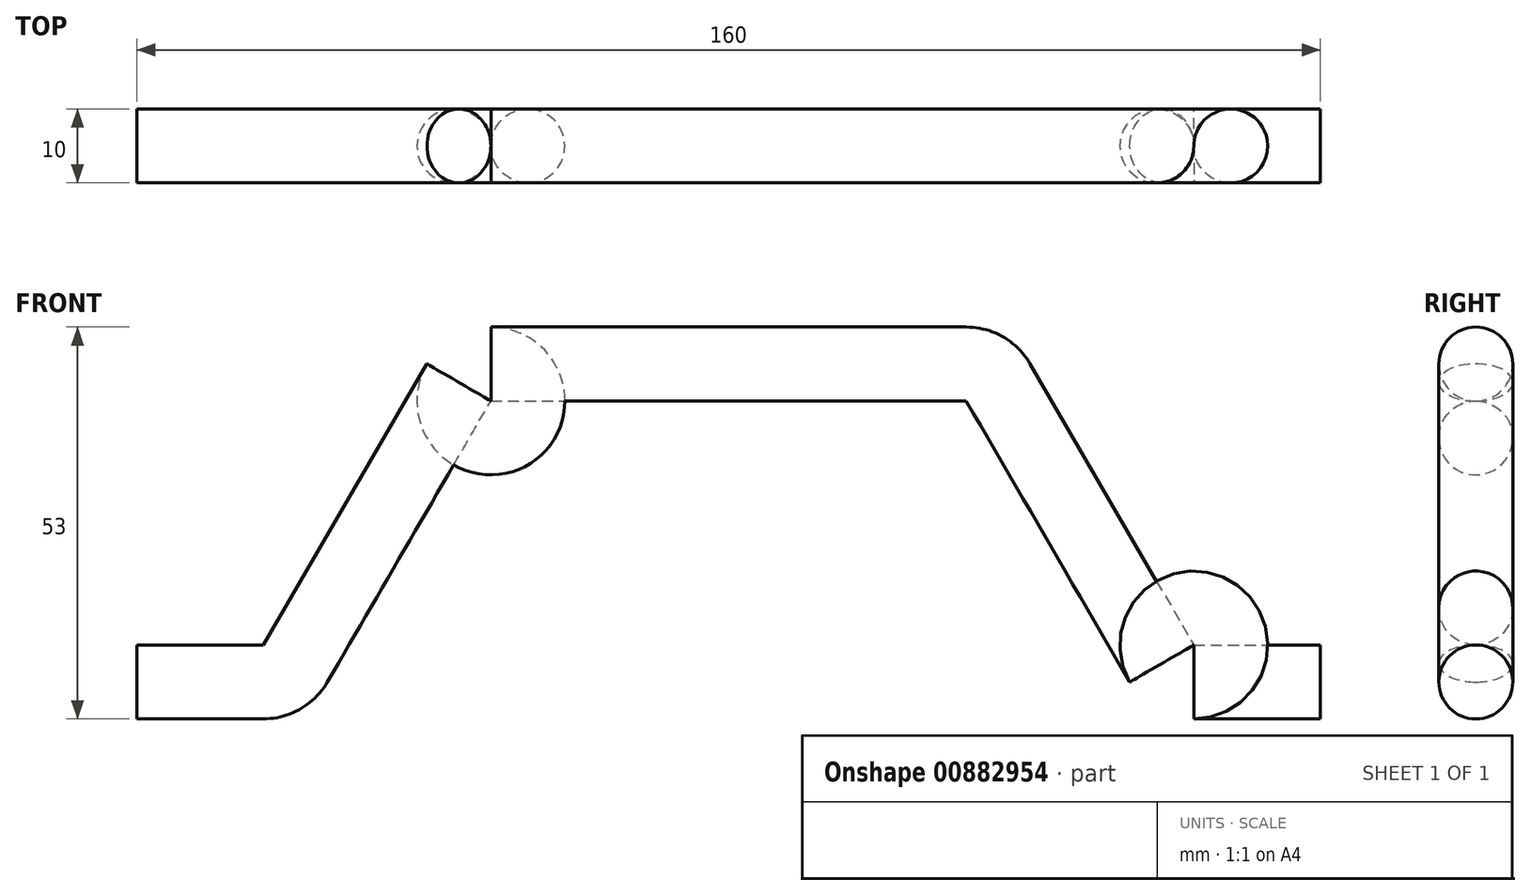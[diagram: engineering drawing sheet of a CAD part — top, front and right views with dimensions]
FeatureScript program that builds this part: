
annotation { "Feature Type Name" : "Feature", "Feature Type Description" : "" }
export const myFeature = defineFeature(function(context is Context, id is Id, definition is map)
    precondition{}
    {
        {
            var Q0;
            Q0=qCreatedBy(makeId("Front.planeOp"),FACE);
            var sketch = newSketch(context, id + "F0", { "sketchPlane" : qUnion([Q0])});
            skLineSegment(sketch, "E0.bottom", {"start": v(0, 0) * mm, "end": v(20, 0) * mm});
            skLineSegment(sketch, "E0.top", {"start": v(0, 5) * mm, "end": v(20, 5) * mm});
            skLineSegment(sketch, "E0.left", {"start": v(0, 0) * mm, "end": v(0, 5) * mm});
            skLineSegment(sketch, "E0.right", {"start": v(20, 0) * mm, "end": v(20, 5) * mm});
            skLineSegment(sketch, "E1.bottom", {"start": v(140, 5) * mm, "end": v(160, 5) * mm});
            skLineSegment(sketch, "E1.top", {"start": v(140, 0) * mm, "end": v(160, 0) * mm});
            skLineSegment(sketch, "E1.left", {"start": v(140, 5) * mm, "end": v(140, 0) * mm});
            skLineSegment(sketch, "E1.right", {"start": v(160, 5) * mm, "end": v(160, 0) * mm});
            skLineSegment(sketch, "E2", {"start": v(-18.53, 0) * mm, "end": v(192.94, 0) * mm, "construction": true});
            skSolve(sketch);
        }
        {
            var Q0;
            Q0=qCreatedBy(makeId("Front.planeOp"),FACE);
            var sketch = newSketch(context, id + "F1", { "sketchPlane" : qUnion([Q0])});
            skLineSegment(sketch, "E3", {"start": v(20, 0) * mm, "end": v(17.12, 4.08) * mm});
            skLineSegment(sketch, "E4", {"start": v(17.12, 4.08) * mm, "end": v(40, 20.24) * mm});
            skLineSegment(sketch, "E5", {"start": v(40, 20.24) * mm, "end": v(42.88, 16.16) * mm});
            skLineSegment(sketch, "E6", {"start": v(42.88, 16.16) * mm, "end": v(20, 0) * mm});
            skLineSegment(sketch, "E7", {"start": v(20, 0) * mm, "end": v(97.93, 55.03) * mm, "construction": true});
            skSolve(sketch);
        }
        {
            var Q0;
            Q0=qCreatedBy(makeId("Front.planeOp"),FACE);
            var sketch = newSketch(context, id + "F2", { "sketchPlane" : qUnion([Q0])});
            skLineSegment(sketch, "E8", {"start": v(140, 0) * mm, "end": v(142.88, 4.08) * mm});
            skLineSegment(sketch, "E9", {"start": v(142.88, 4.08) * mm, "end": v(120, 20.24) * mm});
            skLineSegment(sketch, "E10", {"start": v(120, 20.24) * mm, "end": v(117.12, 16.16) * mm});
            skLineSegment(sketch, "E11", {"start": v(117.12, 16.16) * mm, "end": v(140, 0) * mm});
            skLineSegment(sketch, "E12", {"start": v(140, 0) * mm, "end": v(71.03, 48.7) * mm, "construction": true});
            skSolve(sketch);
        }
        {
            var Q0;
            Q0=qCreatedBy(makeId("Front.planeOp"),FACE);
            var sketch = newSketch(context, id + "F3", { "sketchPlane" : qUnion([Q0])});
            skLineSegment(sketch, "E13.bottom", {"start": v(40, 20.24) * mm, "end": v(120, 20.24) * mm});
            skLineSegment(sketch, "E13.top", {"start": v(40, 15.24) * mm, "end": v(120, 15.24) * mm});
            skLineSegment(sketch, "E13.left", {"start": v(40, 20.24) * mm, "end": v(40, 15.24) * mm});
            skLineSegment(sketch, "E13.right", {"start": v(120, 20.24) * mm, "end": v(120, 15.24) * mm});
            skLineSegment(sketch, "E14", {"start": v(33.87, 15.24) * mm, "end": v(154.92, 15.24) * mm, "construction": true});
            skPoint(sketch, "E14.endSnap0", {"position": v(80, 15.24) * mm});
            skSolve(sketch);
        }
        {
            var Q0;
            Q0=qCreatedBy(makeId("Right.planeOp"),FACE);
            var sketch = newSketch(context, id + "F4", { "sketchPlane" : qUnion([Q0])});
            skCircle(sketch, "E15", {"center": v(0, 0) * mm, "radius": 5 * mm});
            skSolve(sketch);
        }
        {
            var Q0;
            Q0=qCreatedBy(makeId("Front.planeOp"),FACE);
            var sketch = newSketch(context, id + "F5", { "sketchPlane" : qUnion([Q0])});
            skLineSegment(sketch, "E16", {"start": v(0, 0) * mm, "end": v(17.12, 0) * mm});
            skLineSegment(sketch, "E17", {"start": v(21.45, 2.49) * mm, "end": v(43.55, 40.51) * mm});
            skLineSegment(sketch, "E18", {"start": v(47.88, 43) * mm, "end": v(112.12, 43) * mm});
            skLineSegment(sketch, "E19", {"start": v(116.45, 40.51) * mm, "end": v(138.55, 2.49) * mm});
            skLineSegment(sketch, "E20", {"start": v(142.88, 0) * mm, "end": v(160, 0) * mm});
            skPoint(sketch, "E21.visualSharp", {"position": v(20, 0) * mm});
            skArc(sketch, "E21.filletArc", {"start": v(17.12, 0) * mm, "mid": v(19.62, 0.67) * mm, "end": v(21.45, 2.49) * mm});
            skPoint(sketch, "E22.visualSharp", {"position": v(45, 43) * mm});
            skArc(sketch, "E22.filletArc", {"start": v(47.88, 43) * mm, "mid": v(45.38, 42.33) * mm, "end": v(43.55, 40.51) * mm});
            skPoint(sketch, "E23.visualSharp", {"position": v(115, 43) * mm});
            skArc(sketch, "E23.filletArc", {"start": v(116.45, 40.51) * mm, "mid": v(114.62, 42.33) * mm, "end": v(112.12, 43) * mm});
            skPoint(sketch, "E24.visualSharp", {"position": v(140, 0) * mm});
            skArc(sketch, "E24.filletArc", {"start": v(138.55, 2.49) * mm, "mid": v(140.38, 0.67) * mm, "end": v(142.88, 0) * mm});
            skSolve(sketch);
        }
        {
            var Q0;
            Q0=makeQuery(id+"F4.imprint","IMPRINT",FACE,{"disambiguationData":[TD([[makeQuery(id+"F4.imprint","IMPRINT",EDGE,{"derivedFrom":sQuery(id+"F4.wireOp",EDGE,"E15")}),1.0]])]});
            var Q1;
            Q1=sQuery(id+"F5.wireOp",EDGE,"E18");
            var Q2;
            Q2=sQuery(id+"F5.wireOp",EDGE,"E22.filletArc");
            var Q3;
            Q3=sQuery(id+"F5.wireOp",EDGE,"E17");
            var Q4;
            Q4=sQuery(id+"F5.wireOp",EDGE,"E16");
            var Q5;
            Q5=sQuery(id+"F5.wireOp",EDGE,"E21.filletArc");
            var Q6;
            Q6=sQuery(id+"F5.wireOp",EDGE,"E19");
            var Q7;
            Q7=sQuery(id+"F5.wireOp",EDGE,"E23.filletArc");
            var Q8;
            Q8=sQuery(id+"F5.wireOp",EDGE,"E24.filletArc");
            var Q9;
            Q9=sQuery(id+"F5.wireOp",EDGE,"E20");
            sweep(context, id + "F6", {"profiles" : qUnion([Q0]), "path" : qUnion([Q1, Q2, Q3, Q4, Q5, Q6, Q7, Q8, Q9])});
        }
    });
